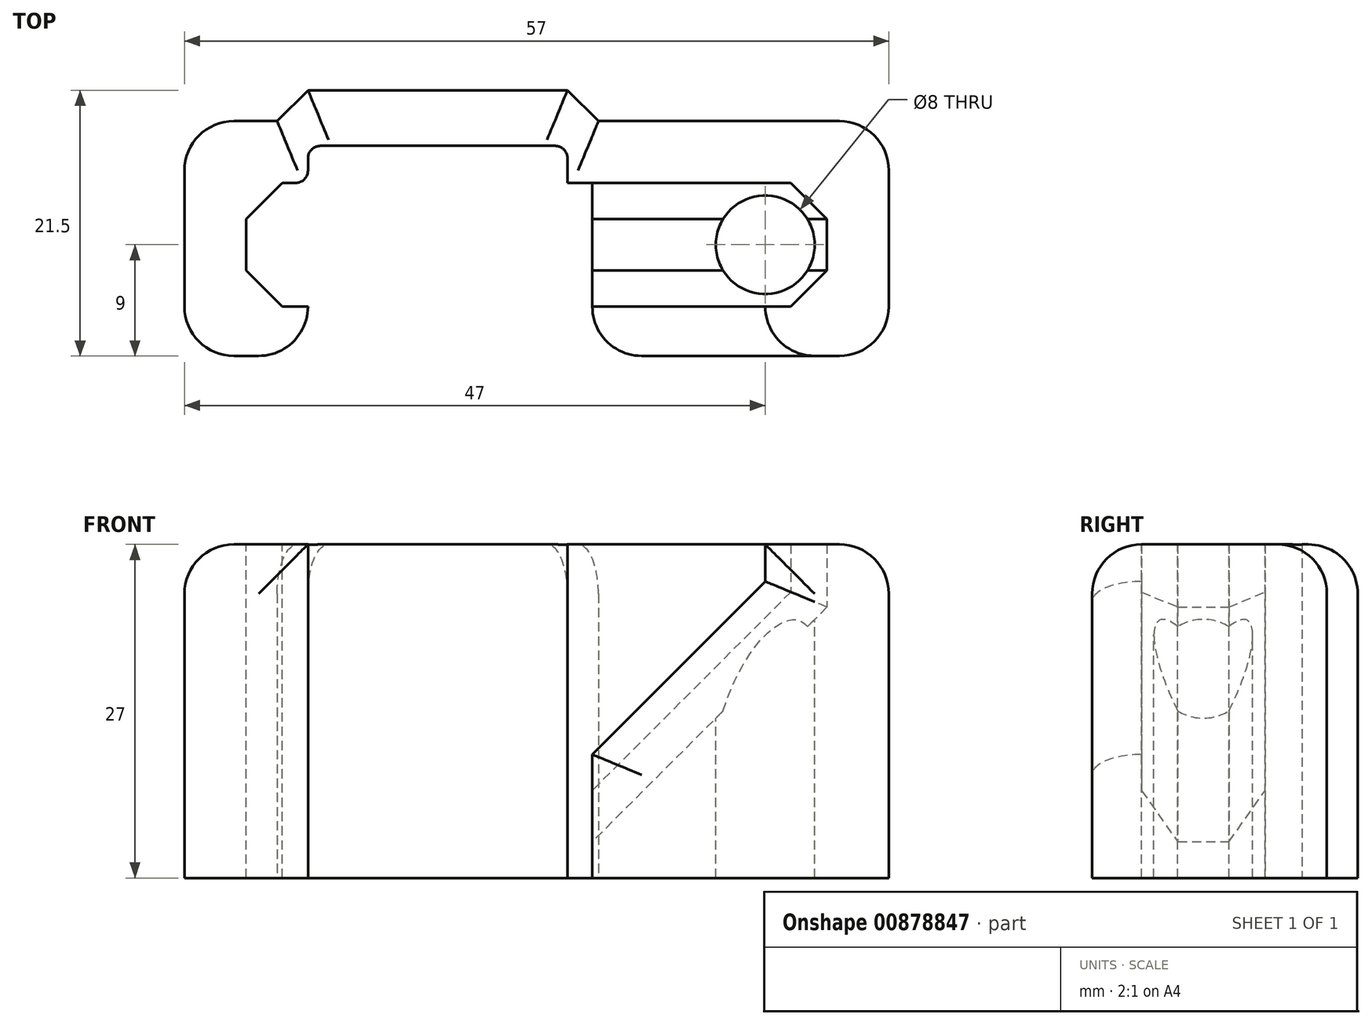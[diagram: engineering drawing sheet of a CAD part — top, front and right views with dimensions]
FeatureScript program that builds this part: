
annotation { "Feature Type Name" : "Feature", "Feature Type Description" : "" }
export const myFeature = defineFeature(function(context is Context, id is Id, definition is map)
    precondition{}
    {
        {
            var Q0;
            Q0=qCreatedBy(makeId("Top.planeOp"),FACE);
            var sketch = newSketch(context, id + "F0", { "sketchPlane" : qUnion([Q0])});
            skLineSegment(sketch, "E0.bottom", {"start": v(0, 0) * mm, "end": v(37, 0) * mm});
            skLineSegment(sketch, "E0.top", {"start": v(0, -17) * mm, "end": v(37, -17) * mm});
            skLineSegment(sketch, "E0.left", {"start": v(0, 0) * mm, "end": v(0, -17) * mm});
            skLineSegment(sketch, "E0.right", {"start": v(37, 0) * mm, "end": v(37, -17) * mm});
            skLineSegment(sketch, "E1.bottom", {"start": v(-10, 0) * mm, "end": v(47, 0) * mm});
            skLineSegment(sketch, "E1.top", {"start": v(-10, -17) * mm, "end": v(47, -17) * mm});
            skLineSegment(sketch, "E1.left", {"start": v(-10, 0) * mm, "end": v(-10, -17) * mm});
            skLineSegment(sketch, "E1.right", {"start": v(47, 0) * mm, "end": v(47, -17) * mm});
            skLineSegment(sketch, "E2.bottom", {"start": v(0, -17) * mm, "end": v(23, -17) * mm});
            skLineSegment(sketch, "E2.top", {"start": v(0, -27) * mm, "end": v(23, -27) * mm});
            skLineSegment(sketch, "E2.left", {"start": v(0, -17) * mm, "end": v(0, -27) * mm});
            skLineSegment(sketch, "E2.right", {"start": v(23, -17) * mm, "end": v(23, -27) * mm});
            skLineSegment(sketch, "E3", {"start": v(23, -17) * mm, "end": v(37, -3) * mm});
            skLineSegment(sketch, "E4.bottom", {"start": v(-10, -17) * mm, "end": v(0, -17) * mm});
            skLineSegment(sketch, "E4.top", {"start": v(-10, -27) * mm, "end": v(0, -27) * mm});
            skLineSegment(sketch, "E4.left", {"start": v(-10, -17) * mm, "end": v(-10, -27) * mm});
            skLineSegment(sketch, "E5.bottom", {"start": v(23, -17) * mm, "end": v(47, -17) * mm});
            skLineSegment(sketch, "E5.top", {"start": v(23, -27) * mm, "end": v(47, -27) * mm});
            skLineSegment(sketch, "E5.right", {"start": v(47, -17) * mm, "end": v(47, -27) * mm});
            skSolve(sketch);
        }
        {
            var Q0;
            {var subQ0=sQuery(id+"F0.wireOp",EDGE,"E2.left");var subQ2=sQuery(id+"F0.wireOp",EDGE,"E0.left");var subQ6=sQuery(id+"F0.wireOp",EDGE,"E2.right");var subQ9=makeQuery(id+"F0.imprint","IMPRINT",EDGE,{"derivedFrom":subQ0});var subQ10=makeQuery(id+"F0.imprint","IMPRINT",EDGE,{"derivedFrom":subQ6});var subQ14=sQuery(id+"F0.wireOp",EDGE,"E1.right");var subQ17=sQuery(id+"F0.wireOp",EDGE,"E0.bottom");var subQ24=makeQuery(id+"F0.imprint","IMPRINT",EDGE,{"derivedFrom":subQ2});Q0=qUnion([makeQuery(id+"F0.imprint","IMPRINT",FACE,{"disambiguationData":[TD([[makeQuery(id+"F0.imprint","IMPRINT",EDGE,{"derivedFrom":subQ17}),-1.0]])]}),makeQuery(id+"F0.imprint","IMPRINT",FACE,{"disambiguationData":[TD([[subQ24,-1.0]])]}),makeQuery(id+"F0.imprint","IMPRINT",FACE,{"disambiguationData":[TD([[subQ10,1.0]])]}),makeQuery(id+"F0.imprint","IMPRINT",FACE,{"disambiguationData":[TD([[subQ9,-1.0]])]}),makeQuery(id+"F0.imprint","IMPRINT",FACE,{"disambiguationData":[TD([[makeQuery(id+"F0.imprint","IMPRINT",EDGE,{"derivedFrom":subQ14}),-1.0]])]}),makeQuery(id+"F0.imprint","IMPRINT",FACE,{"disambiguationData":[TD([[makeQuery(id+"F0.imprint","IMPRINT",EDGE,{"derivedFrom":sQuery(id+"F0.wireOp",EDGE,"E2.top")}),1.0]])]})]);}
            var Q1;
            {var subQ3=sQuery(id+"F0.wireOp",EDGE,"E3");Q1=makeQuery(id+"F0.imprint","IMPRINT",FACE,{"disambiguationData":[TD([[makeQuery(id+"F0.imprint","IMPRINT",EDGE,{"derivedFrom":subQ3}),-1.0]])]});}
            extrude(context, id + "F1", {"entities" : qUnion([Q0, Q1]), "oppositeDirection" : true, "depth" : 5 * mm, "offsetDistance" : 25 * mm});
        }
        {
            var Q0;
            {var subQ0=sQuery(id+"F0.wireOp",EDGE,"E0.left");Q0=makeQuery(id+"F0.imprint","IMPRINT",FACE,{"disambiguationData":[TD([[makeQuery(id+"F0.imprint","IMPRINT",EDGE,{"derivedFrom":subQ0}),-1.0]])]});}
            var Q1;
            {var subQ3=sQuery(id+"F0.wireOp",EDGE,"E1.right");Q1=makeQuery(id+"F0.imprint","IMPRINT",FACE,{"disambiguationData":[TD([[makeQuery(id+"F0.imprint","IMPRINT",EDGE,{"derivedFrom":subQ3}),-1.0]])]});}
            var Q2;
            {var subQ3=sQuery(id+"F0.wireOp",EDGE,"E3");Q2=makeQuery(id+"F0.imprint","IMPRINT",FACE,{"disambiguationData":[TD([[makeQuery(id+"F0.imprint","IMPRINT",EDGE,{"derivedFrom":subQ3}),-1.0]])]});}
            var Q3;
            {var subQ0=sQuery(id+"F0.wireOp",EDGE,"E2.right");Q3=makeQuery(id+"F0.imprint","IMPRINT",FACE,{"disambiguationData":[TD([[makeQuery(id+"F0.imprint","IMPRINT",EDGE,{"derivedFrom":subQ0}),1.0]])]});}
            var Q4;
            {var subQ0=sQuery(id+"F0.wireOp",EDGE,"E2.left");Q4=makeQuery(id+"F0.imprint","IMPRINT",FACE,{"disambiguationData":[TD([[makeQuery(id+"F0.imprint","IMPRINT",EDGE,{"derivedFrom":subQ0}),-1.0]])]});}
            extrude(context, id + "F2", {"entities" : qUnion([Q0, Q1, Q2, Q3, Q4]), "operationType" : NewBodyOperationType.ADD, "depth" : 14 * mm, "offsetDistance" : 25 * mm});
        }
        {
            var Q0;
            {var subQ0=sQuery(id+"F0.wireOp",EDGE,"E1.bottom");var subQ1=sQuery(id+"F0.wireOp",EDGE,"E0.bottom");Q0=makeQuery(id+"F2.boolean.opBoolean","MERGE",FACE,{"derivedFrom":[makeQuery(id+"F1.opExtrude","SWEPT_FACE",FACE,{"disambiguationData":[OSD([subQ1,subQ0])]}),makeQuery(id+"F2.opExtrude","SWEPT_FACE",FACE,{"disambiguationData":[OSD([subQ0]),TDD([makeQuery(id+"F0.imprint","IMPRINT",EDGE,{"disambiguationData":[TD([[makeQuery(id+"F0.imprint","INTERSECT",VERTEX,{"derivedFrom":[subQ0,sQuery(id+"F0.wireOp",EDGE,"E1.right")]}),1.0]])],"derivedFrom":subQ0})])]}),makeQuery(id+"F2.opExtrude","SWEPT_FACE",FACE,{"disambiguationData":[OSD([subQ0]),TDD([makeQuery(id+"F0.imprint","IMPRINT",EDGE,{"disambiguationData":[TD([[makeQuery(id+"F0.imprint","INTERSECT",VERTEX,{"derivedFrom":[subQ0,sQuery(id+"F0.wireOp",EDGE,"E1.left")]}),-1.0]])],"derivedFrom":subQ0})])]})]});}
            var sketch = newSketch(context, id + "F3", { "sketchPlane" : qUnion([Q0])});
            skArc(sketch, "E6", {"start": v(0, 0) * mm, "mid": v(5, 5) * mm, "end": v(0, 10) * mm, "construction": true});
            skLineSegment(sketch, "E7", {"start": v(5, 5) * mm, "end": v(5, 32.74) * mm, "construction": true});
            skLineSegment(sketch, "E8", {"start": v(5, 5) * mm, "end": v(5, -17.27) * mm, "construction": true});
            skLineSegment(sketch, "E9", {"start": v(5, 2.93) * mm, "end": v(5, 7.07) * mm});
            skLineSegment(sketch, "E10", {"start": v(5, 7.07) * mm, "end": v(2.07, 10) * mm});
            skLineSegment(sketch, "E11", {"start": v(2.07, 10) * mm, "end": v(0, 10) * mm});
            skLineSegment(sketch, "E12", {"start": v(5, 2.93) * mm, "end": v(2.07, 0) * mm});
            skLineSegment(sketch, "E13", {"start": v(2.07, 0) * mm, "end": v(0, 0) * mm});
            skLineSegment(sketch, "E14", {"start": v(-18.5, 0) * mm, "end": v(-18.5, 42.34) * mm, "construction": true});
            skLineSegment(sketch, "E15.MirrorCS", {"start": v(-39.07, 0) * mm, "end": v(-37, 0) * mm});
            skLineSegment(sketch, "E16.MirrorCS", {"start": v(-42, 2.93) * mm, "end": v(-39.07, 0) * mm});
            skLineSegment(sketch, "E17.MirrorCS", {"start": v(-42, 5) * mm, "end": v(-42, 32.74) * mm, "construction": true});
            skLineSegment(sketch, "E18.MirrorCS", {"start": v(-42, 7.07) * mm, "end": v(-39.07, 10) * mm});
            skLineSegment(sketch, "E19.MirrorCS", {"start": v(-39.07, 10) * mm, "end": v(-37, 10) * mm});
            skLineSegment(sketch, "E20", {"start": v(-42, 2.93) * mm, "end": v(-42, 7.07) * mm});
            skLineSegment(sketch, "E21", {"start": v(-37, 10) * mm, "end": v(-37, 0) * mm});
            skLineSegment(sketch, "E22", {"start": v(-42, 5) * mm, "end": v(-37, 5) * mm, "construction": true});
            skCircle(sketch, "E23", {"center": v(-37, 5) * mm, "radius": 4 * mm});
            skSolve(sketch);
        }
        {
            var Q0;
            Q0=makeQuery(id+"F3.imprint","IMPRINT",FACE,{"disambiguationData":[TD([[makeQuery(id+"F3.imprint","IMPRINT",EDGE,{"derivedFrom":sQuery(id+"F3.wireOp",EDGE,"E9")}),1.0]])]});
            extrude(context, id + "F4", {"entities" : qUnion([Q0]), "operationType" : NewBodyOperationType.REMOVE, "oppositeDirection" : true, "depth" : 35 * mm, "offsetDistance" : 25 * mm});
        }
        {
            var Q0;
            Q0=makeQuery(id+"F2.opExtrude","CAP_FACE",FACE,{"disambiguationData":[OSD([sQuery(id+"F0.wireOp",EDGE,"E0.right"),sQuery(id+"F0.wireOp",EDGE,"E1.bottom"),sQuery(id+"F0.wireOp",EDGE,"E1.right"),sQuery(id+"F0.wireOp",EDGE,"E2.right"),sQuery(id+"F0.wireOp",EDGE,"E3"),sQuery(id+"F0.wireOp",EDGE,"E5.top"),sQuery(id+"F0.wireOp",EDGE,"E5.right")])],"isStart":false});
            cPlane(context, id + "F5", {"entities" : qUnion([Q0]), "cplaneType" : CPlaneType.OFFSET, "offset" : 9.5 * mm, "oppositeDirection" : true, "width" : 150 * mm, "height" : 150 * mm});
        }
        {
            var Q0;
            Q0=qCreatedBy(id+"F5.planeOp",FACE);
            var sketch = newSketch(context, id + "F6", { "sketchPlane" : qUnion([Q0])});
            skLineSegment(sketch, "E24", {"start": v(37, 0) * mm, "end": v(37, -3) * mm});
            skLineSegment(sketch, "E25", {"start": v(37, -3) * mm, "end": v(23, -17) * mm});
            skLineSegment(sketch, "E26", {"start": v(23, -17) * mm, "end": v(19.4, -20.6) * mm});
            skSolve(sketch);
        }
        {
            var Q0;
            Q0=makeQuery(id+"F3.imprint","IMPRINT",FACE,{"disambiguationData":[TD([[makeQuery(id+"F3.imprint","IMPRINT",EDGE,{"derivedFrom":sQuery(id+"F3.wireOp",EDGE,"E15.MirrorCS")}),1.0]])]});
            var Q1;
            {var subQ0=sQuery(id+"F3.wireOp",EDGE,"E23");var subQ1=sQuery(id+"F3.wireOp",EDGE,"E21");var subQ2=makeQuery(id+"F3.imprint","INTERSECT",VERTEX,{"disambiguationData":[OD(0.0)],"derivedFrom":[subQ1,subQ0]});Q1=makeQuery(id+"F3.imprint","IMPRINT",FACE,{"disambiguationData":[TD([[makeQuery(id+"F3.imprint","IMPRINT",EDGE,{"disambiguationData":[TD([[subQ2,-1.0]])],"derivedFrom":subQ1}),-1.0]])]});}
            var Q2;
            Q2 = qConstructionFilter(qBodyType(qCreatedBy(id + "F6" ,EDGE), BodyType.WIRE), ConstructionObject.NO);
            sweep(context, id + "F7", {"operationType" : NewBodyOperationType.REMOVE, "profiles" : qUnion([Q0, Q1]), "path" : qUnion([Q2])});
        }
        {
            var Q0;
            {var subQ0=sQuery(id+"F3.wireOp",EDGE,"E23");var subQ1=sQuery(id+"F3.wireOp",EDGE,"E21");var subQ2=makeQuery(id+"F3.imprint","INTERSECT",VERTEX,{"disambiguationData":[OD(0.0)],"derivedFrom":[subQ1,subQ0]});Q0=makeQuery(id+"F3.imprint","IMPRINT",FACE,{"disambiguationData":[TD([[makeQuery(id+"F3.imprint","IMPRINT",EDGE,{"disambiguationData":[TD([[subQ2,-1.0]])],"derivedFrom":subQ1}),1.0]])]});}
            var Q1;
            {var subQ0=sQuery(id+"F3.wireOp",EDGE,"E23");var subQ1=sQuery(id+"F3.wireOp",EDGE,"E21");var subQ2=makeQuery(id+"F3.imprint","INTERSECT",VERTEX,{"disambiguationData":[OD(0.0)],"derivedFrom":[subQ1,subQ0]});Q1=makeQuery(id+"F3.imprint","IMPRINT",FACE,{"disambiguationData":[TD([[makeQuery(id+"F3.imprint","IMPRINT",EDGE,{"disambiguationData":[TD([[subQ2,-1.0]])],"derivedFrom":subQ1}),-1.0]])]});}
            extrude(context, id + "F8", {"entities" : qUnion([Q0, Q1]), "operationType" : NewBodyOperationType.REMOVE, "endBound" : BoundingType.THROUGH_ALL, "oppositeDirection" : true, "depth" : 30 * mm, "offsetDistance" : 25 * mm, "hasSecondDirection" : true, "secondDirectionOppositeDirection" : false, "secondDirectionDepth" : 35 * mm});
        }
        {
            var Q0;
            {var subQ0=sQuery(id+"F0.wireOp",EDGE,"E4.left");var subQ1=sQuery(id+"F0.wireOp",EDGE,"E1.left");Q0=makeQuery(id+"F2.boolean.opBoolean","MERGE",FACE,{"derivedFrom":[makeQuery(id+"F1.opExtrude","SWEPT_FACE",FACE,{"disambiguationData":[OSD([subQ1,subQ0])]}),makeQuery(id+"F2.opExtrude","SWEPT_FACE",FACE,{"disambiguationData":[OSD([subQ1,subQ0])]})]});}
            cPlane(context, id + "F9", {"entities" : qUnion([Q0]), "cplaneType" : CPlaneType.OFFSET, "offset" : 10 * mm, "oppositeDirection" : true, "width" : 150 * mm, "height" : 150 * mm});
        }
        {
            var Q0;
            Q0=qCreatedBy(id+"F9.planeOp",FACE);
            var sketch = newSketch(context, id + "F10", { "sketchPlane" : qUnion([Q0])});
            skLineSegment(sketch, "E27", {"start": v(27, 0) * mm, "end": v(0, 0) * mm});
            skLineSegment(sketch, "E28", {"start": v(0, 0) * mm, "end": v(0, -3) * mm});
            skLineSegment(sketch, "E29", {"start": v(0, -3) * mm, "end": v(27, -3) * mm});
            skLineSegment(sketch, "E30", {"start": v(27, -3) * mm, "end": v(27, 0) * mm});
            skSolve(sketch);
        }
        {
            var Q0;
            Q0 = qSketchRegion(id + "F10", true);
            extrude(context, id + "F11", {"entities" : qUnion([Q0]), "operationType" : NewBodyOperationType.REMOVE, "oppositeDirection" : true, "depth" : 21 * mm, "offsetDistance" : 25 * mm});
        }
        {
            var Q0;
            {var subQ0=sQuery(id+"F0.wireOp",EDGE,"E5.top");var subQ1=sQuery(id+"F0.wireOp",EDGE,"E4.top");Q0=makeQuery(id+"F2.boolean.opBoolean","MERGE",FACE,{"derivedFrom":[makeQuery(id+"F1.opExtrude","SWEPT_FACE",FACE,{"disambiguationData":[OSD([sQuery(id+"F0.wireOp",EDGE,"E2.top"),subQ1,subQ0])]}),makeQuery(id+"F2.opExtrude","SWEPT_FACE",FACE,{"disambiguationData":[OSD([subQ1])]}),makeQuery(id+"F2.opExtrude","SWEPT_FACE",FACE,{"disambiguationData":[OSD([subQ0])]})]});}
            var sketch = newSketch(context, id + "F12", { "sketchPlane" : qUnion([Q0])});
            skLineSegment(sketch, "E31", {"start": v(23.5, -5) * mm, "end": v(21, -7.5) * mm});
            skLineSegment(sketch, "E32", {"start": v(21, -7.5) * mm, "end": v(0, -7.5) * mm});
            skLineSegment(sketch, "E33", {"start": v(0, -7.5) * mm, "end": v(-2.5, -5) * mm});
            skSolve(sketch);
        }
        {
            var Q0;
            {var subQ0=sQuery(id+"F12.wireOp",EDGE,"E31");Q0=makeQuery(id+"F12.imprint","IMPRINT",FACE,{"disambiguationData":[TD([[makeQuery(id+"F12.imprint","IMPRINT",EDGE,{"derivedFrom":subQ0}),-1.0]])]});}
            var Q1;
            {var subQ0=sQuery(id+"F0.wireOp",EDGE,"E1.bottom");var subQ1=sQuery(id+"F0.wireOp",EDGE,"E0.bottom");Q1=makeQuery(id+"F2.boolean.opBoolean","MERGE",FACE,{"derivedFrom":[makeQuery(id+"F1.opExtrude","SWEPT_FACE",FACE,{"disambiguationData":[OSD([subQ1,subQ0])]}),makeQuery(id+"F2.opExtrude","SWEPT_FACE",FACE,{"disambiguationData":[OSD([subQ0]),TDD([makeQuery(id+"F0.imprint","IMPRINT",EDGE,{"disambiguationData":[TD([[makeQuery(id+"F0.imprint","INTERSECT",VERTEX,{"derivedFrom":[subQ0,sQuery(id+"F0.wireOp",EDGE,"E1.right")]}),1.0]])],"derivedFrom":subQ0})])]}),makeQuery(id+"F2.opExtrude","SWEPT_FACE",FACE,{"disambiguationData":[OSD([subQ0]),TDD([makeQuery(id+"F0.imprint","IMPRINT",EDGE,{"disambiguationData":[TD([[makeQuery(id+"F0.imprint","INTERSECT",VERTEX,{"derivedFrom":[subQ0,sQuery(id+"F0.wireOp",EDGE,"E1.left")]}),-1.0]])],"derivedFrom":subQ0})])]})]});}
            extrude(context, id + "F13", {"entities" : qUnion([Q0]), "operationType" : NewBodyOperationType.ADD, "endBound" : BoundingType.UP_TO_SURFACE, "oppositeDirection" : true, "depth" : 25 * mm, "endBoundEntityFace" : qUnion([Q1]), "offsetDistance" : 25 * mm});
        }
        {
            var Q0;
            Q0=makeQuery(id+"F11.boolean.opBoolean","COPY",EDGE,{"derivedFrom":makeQuery(id+"F11.opExtrude","CAP_EDGE",EDGE,{"disambiguationData":[OSD([sQuery(id+"F10.wireOp",EDGE,"E27")])],"isStart":true})});
            var Q1;
            Q1=makeQuery(id+"F11.boolean.opBoolean","COPY",EDGE,{"derivedFrom":makeQuery(id+"F11.opExtrude","CAP_EDGE",EDGE,{"disambiguationData":[OSD([sQuery(id+"F10.wireOp",EDGE,"E27")])],"isStart":false})});
            var Q2;
            Q2=makeQuery(id+"F11.boolean.opBoolean","COPY",EDGE,{"derivedFrom":makeQuery(id+"F11.opExtrude","CAP_EDGE",EDGE,{"disambiguationData":[OSD([sQuery(id+"F10.wireOp",EDGE,"E29")])],"isStart":false})});
            var Q3;
            Q3=makeQuery(id+"F11.boolean.opBoolean","COPY",EDGE,{"derivedFrom":makeQuery(id+"F11.opExtrude","CAP_EDGE",EDGE,{"disambiguationData":[OSD([sQuery(id+"F10.wireOp",EDGE,"E29")])],"isStart":true})});
            fillet(context, id + "F14", {"entities" : qUnion([Q0, Q1, Q2, Q3]), "radius" : 1 * mm, "tangentPropagation" : true, "allowEdgeOverflow" : false});
        }
        {
            var Q0;
            {var subQ0=sQuery(id+"F0.wireOp",EDGE,"E1.left");var subQ1=sQuery(id+"F0.wireOp",EDGE,"E1.bottom");Q0=makeQuery(id+"F2.boolean.opBoolean","MERGE",EDGE,{"derivedFrom":[makeQuery(id+"F1.opExtrude","SWEPT_EDGE",EDGE,{"disambiguationData":[OSD([subQ1,subQ0])]}),makeQuery(id+"F2.opExtrude","SWEPT_EDGE",EDGE,{"disambiguationData":[OSD([subQ1,subQ0])]})]});}
            var Q1;
            {var subQ0=sQuery(id+"F0.wireOp",EDGE,"E1.right");var subQ1=sQuery(id+"F0.wireOp",EDGE,"E1.bottom");Q1=makeQuery(id+"F2.boolean.opBoolean","MERGE",EDGE,{"derivedFrom":[makeQuery(id+"F1.opExtrude","SWEPT_EDGE",EDGE,{"disambiguationData":[OSD([subQ1,subQ0])]}),makeQuery(id+"F2.opExtrude","SWEPT_EDGE",EDGE,{"disambiguationData":[OSD([subQ1,subQ0])]})]});}
            var Q2;
            {var subQ0=sQuery(id+"F0.wireOp",EDGE,"E1.bottom");Q2=makeQuery(id+"F2.opExtrude","CAP_EDGE",EDGE,{"disambiguationData":[OSD([subQ0]),TDD([makeQuery(id+"F0.imprint","IMPRINT",EDGE,{"disambiguationData":[TD([[makeQuery(id+"F0.imprint","INTERSECT",VERTEX,{"derivedFrom":[subQ0,sQuery(id+"F0.wireOp",EDGE,"E1.right")]}),1.0]])],"derivedFrom":subQ0})])],"isStart":false});}
            var Q3;
            Q3=makeQuery(id+"F2.opExtrude","CAP_EDGE",EDGE,{"disambiguationData":[OSD([sQuery(id+"F0.wireOp",EDGE,"E1.right"),sQuery(id+"F0.wireOp",EDGE,"E5.right")])],"isStart":false});
            var Q4;
            Q4=makeQuery(id+"F1.opExtrude","CAP_EDGE",EDGE,{"disambiguationData":[OSD([sQuery(id+"F0.wireOp",EDGE,"E1.right"),sQuery(id+"F0.wireOp",EDGE,"E5.right")])],"isStart":false});
            var Q5;
            Q5=makeQuery(id+"F2.opExtrude","CAP_EDGE",EDGE,{"disambiguationData":[OSD([sQuery(id+"F0.wireOp",EDGE,"E1.left"),sQuery(id+"F0.wireOp",EDGE,"E4.left")])],"isStart":false});
            var Q6;
            {var subQ0=sQuery(id+"F0.wireOp",EDGE,"E1.bottom");Q6=makeQuery(id+"F2.opExtrude","CAP_EDGE",EDGE,{"disambiguationData":[OSD([subQ0]),TDD([makeQuery(id+"F0.imprint","IMPRINT",EDGE,{"disambiguationData":[TD([[makeQuery(id+"F0.imprint","INTERSECT",VERTEX,{"derivedFrom":[subQ0,sQuery(id+"F0.wireOp",EDGE,"E1.left")]}),-1.0]])],"derivedFrom":subQ0})])],"isStart":false});}
            var Q7;
            Q7=makeQuery(id+"F2.opExtrude","CAP_EDGE",EDGE,{"disambiguationData":[OSD([sQuery(id+"F0.wireOp",EDGE,"E0.left"),sQuery(id+"F0.wireOp",EDGE,"E2.left")])],"isStart":false});
            var Q8;
            Q8=makeQuery(id+"F1.opExtrude","CAP_EDGE",EDGE,{"disambiguationData":[OSD([sQuery(id+"F0.wireOp",EDGE,"E1.left"),sQuery(id+"F0.wireOp",EDGE,"E4.left")])],"isStart":false});
            var Q9;
            Q9=makeQuery(id+"F2.opExtrude","CAP_EDGE",EDGE,{"disambiguationData":[OSD([sQuery(id+"F0.wireOp",EDGE,"E0.right")])],"isStart":false});
            var Q10;
            Q10=makeQuery(id+"F2.opExtrude","CAP_EDGE",EDGE,{"disambiguationData":[OSD([sQuery(id+"F0.wireOp",EDGE,"E3")])],"isStart":false});
            var Q11;
            Q11=makeQuery(id+"F2.opExtrude","CAP_EDGE",EDGE,{"disambiguationData":[OSD([sQuery(id+"F0.wireOp",EDGE,"E2.right")])],"isStart":false});
            var Q12;
            {var subQ2=sQuery(id+"F0.wireOp",EDGE,"E1.bottom");var subQ3=sQuery(id+"F0.wireOp",EDGE,"E0.bottom");var subQ8=sQuery(id+"F12.wireOp",EDGE,"E31");Q12=makeQuery(id+"F13.boolean.opBoolean","SPLIT",EDGE,{"disambiguationData":[TD([makeQuery(id+"F13.opExtrude","SWEPT_FACE",FACE,{"disambiguationData":[OSD([subQ8])]})])],"derivedFrom":makeQuery(id+"F1.opExtrude","CAP_EDGE",EDGE,{"disambiguationData":[OSD([subQ3,subQ2])],"isStart":false})});}
            var Q13;
            Q13=makeQuery(id+"F13.opExtrude","CAP_EDGE",EDGE,{"disambiguationData":[OSD([sQuery(id+"F12.wireOp",EDGE,"E31")])],"isStart":false});
            var Q14;
            Q14=makeQuery(id+"F13.opExtrude","CAP_EDGE",EDGE,{"disambiguationData":[OSD([sQuery(id+"F12.wireOp",EDGE,"E32")])],"isStart":false});
            var Q15;
            Q15=makeQuery(id+"F13.opExtrude","CAP_EDGE",EDGE,{"disambiguationData":[OSD([sQuery(id+"F12.wireOp",EDGE,"E33")])],"isStart":false});
            var Q16;
            {var subQ2=sQuery(id+"F0.wireOp",EDGE,"E1.bottom");var subQ3=sQuery(id+"F0.wireOp",EDGE,"E0.bottom");var subQ8=sQuery(id+"F12.wireOp",EDGE,"E33");Q16=makeQuery(id+"F13.boolean.opBoolean","SPLIT",EDGE,{"disambiguationData":[TD([makeQuery(id+"F13.opExtrude","SWEPT_FACE",FACE,{"disambiguationData":[OSD([subQ8])]})])],"derivedFrom":makeQuery(id+"F1.opExtrude","CAP_EDGE",EDGE,{"disambiguationData":[OSD([subQ3,subQ2])],"isStart":false})});}
            fillet(context, id + "F15", {"entities" : qUnion([Q0, Q1, Q2, Q3, Q4, Q5, Q6, Q7, Q8, Q9, Q10, Q11, Q12, Q13, Q14, Q15, Q16]), "radius" : 4 * mm, "tangentPropagation" : true, "allowEdgeOverflow" : false});
        }
        {
            var Q0;
            Q0=makeQuery(id+"F1.opExtrude","SWEPT_BODY",BODY,{"disambiguationData":[OSD([sQuery(id+"F0.wireOp",EDGE,"E0.bottom"),sQuery(id+"F0.wireOp",EDGE,"E1.bottom"),sQuery(id+"F0.wireOp",EDGE,"E1.left"),sQuery(id+"F0.wireOp",EDGE,"E1.right"),sQuery(id+"F0.wireOp",EDGE,"E2.top"),sQuery(id+"F0.wireOp",EDGE,"E4.top"),sQuery(id+"F0.wireOp",EDGE,"E4.left"),sQuery(id+"F0.wireOp",EDGE,"E5.top"),sQuery(id+"F0.wireOp",EDGE,"E5.right")])]});
            var Q1;
            Q1=makeQuery(id+"F13.opExtrude","CAP_EDGE",EDGE,{"disambiguationData":[OSD([sQuery(id+"F12.wireOp",EDGE,"E32")])],"isStart":true});
            transform(context, id + "F16", {"entities" : qUnion([Q0]), "transformType" : TransformType.ROTATION, "transformAxis" : qUnion([Q1]), "angle" : 270 * degree, "makeCopy" : false});
        }
    });
